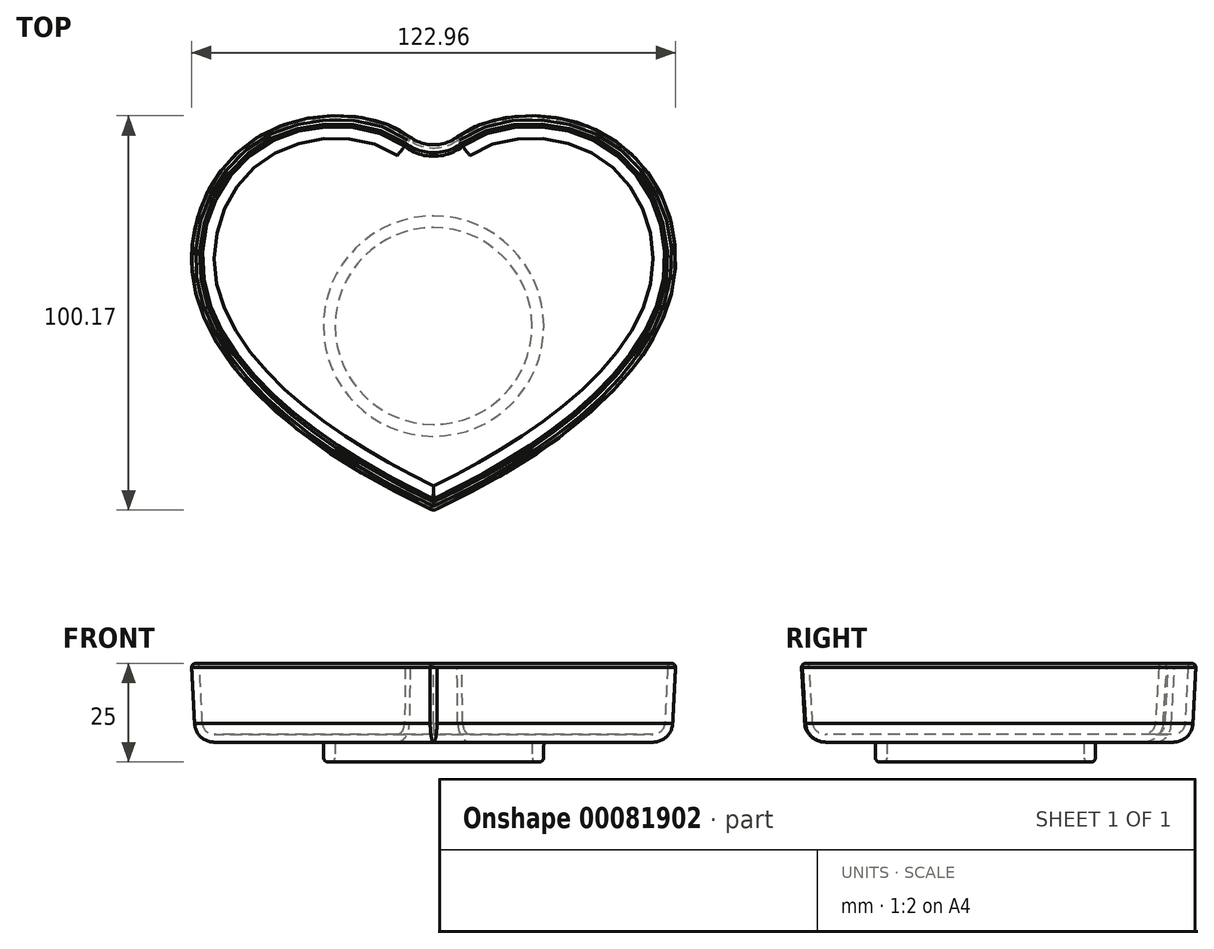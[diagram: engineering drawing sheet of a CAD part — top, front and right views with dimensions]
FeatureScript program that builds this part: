
annotation { "Feature Type Name" : "Feature", "Feature Type Description" : "" }
export const myFeature = defineFeature(function(context is Context, id is Id, definition is map)
    precondition{}
    {
        {
            var Q0;
            Q0=qCreatedBy(makeId("Top.planeOp"),FACE);
            var sketch = newSketch(context, id + "F0", { "sketchPlane" : qUnion([Q0])});
            skLineSegment(sketch, "E0", {"start": v(0, 0) * mm, "end": v(0, 80) * mm, "construction": true});
            skFitSpline(sketch, "E1", {"points": [v(0, 80) * mm, v(-38, 96) * mm, v(-60, 57) * mm, v(0, 0) * mm], "startDerivative": vector(0, 176.4) * mm, "endDerivative": vector(234.37, -109.86) * mm});
            skFitSpline(sketch, "E2.MirrorCS", {"points": [v(0, 80) * mm, v(38, 96) * mm, v(60, 57) * mm, v(0, 0) * mm], "startDerivative": vector(0, 176.4) * mm, "endDerivative": vector(-234.37, -109.86) * mm});
            skSolve(sketch);
        }
        {
            var Q0;
            Q0 = qSketchRegion(id + "F0", true);
            extrude(context, id + "F1", {"entities" : qUnion([Q0]), "depth" : 20 * mm, "hasDraft" : true, "draftAngle" : 3 * degree});
        }
        {
            var Q0;
            {var subQ0=sQuery(id+"F0.wireOp",EDGE,"E2.MirrorCS");var subQ1=sQuery(id+"F0.wireOp",EDGE,"E1");Q0=makeQuery(id+"F1.opExtrude","SWEPT_EDGE",EDGE,{"disambiguationData":[OSD([subQ1,subQ0]),TDD([makeQuery(id+"F0.imprint","INTERSECT",VERTEX,{"disambiguationData":[OD(0.0)],"derivedFrom":[subQ1,subQ0]})])]});}
            fillet(context, id + "F2", {"entities" : qUnion([Q0]), "radius" : 2 * mm, "tangentPropagation" : true, "rho" : 0.5, "crossSection" : FilletCrossSection.CONIC, "allowEdgeOverflow" : false});
        }
        {
            var Q0;
            {var subQ0=sQuery(id+"F0.wireOp",EDGE,"E2.MirrorCS");var subQ1=sQuery(id+"F0.wireOp",EDGE,"E1");Q0=makeQuery(id+"F1.opExtrude","SWEPT_EDGE",EDGE,{"disambiguationData":[OSD([subQ1,subQ0]),TDD([makeQuery(id+"F0.imprint","INTERSECT",VERTEX,{"disambiguationData":[OD(1.0)],"derivedFrom":[subQ1,subQ0]})])]});}
            fillet(context, id + "F3", {"entities" : qUnion([Q0]), "radius" : 10 * mm, "tangentPropagation" : true, "allowEdgeOverflow" : false});
        }
        {
            var Q0;
            Q0=makeQuery(id+"F1.opExtrude","CAP_FACE",FACE,{"disambiguationData":[OSD([sQuery(id+"F0.wireOp",EDGE,"E1"),sQuery(id+"F0.wireOp",EDGE,"E2.MirrorCS")])],"isStart":false});
            shell(context, id + "F4", {"entities" : qUnion([Q0]), "thickness" : 2 * mm});
        }
        {
            var Q0;
            {var subQ0=sQuery(id+"F0.wireOp",EDGE,"E1");Q0=makeQuery(id+"F4.opShell","OFFSET_EDGE",EDGE,{"disambiguationData":[OSD([subQ0]),TDD([makeQuery(id+"F1.opExtrude","CAP_EDGE",EDGE,{"disambiguationData":[OSD([subQ0])],"isStart":true})])]});}
            fillet(context, id + "F5", {"entities" : qUnion([Q0]), "radius" : 3 * mm, "tangentPropagation" : true, "allowEdgeOverflow" : false});
        }
        {
            var Q0;
            Q0=makeQuery(id+"F1.opExtrude","CAP_EDGE",EDGE,{"disambiguationData":[OSD([sQuery(id+"F0.wireOp",EDGE,"E1")])],"isStart":true});
            var Q1;
            {var subQ0=sQuery(id+"F0.wireOp",EDGE,"E2.MirrorCS");var subQ1=sQuery(id+"F0.wireOp",EDGE,"E1");Q1=makeQuery(id+"F3.opFillet","BLEND_EDGE",EDGE,{"blendedFrom":[makeQuery(id+"F1.opExtrude","SWEPT_EDGE",EDGE,{"disambiguationData":[OSD([subQ1,subQ0]),TDD([makeQuery(id+"F0.imprint","INTERSECT",VERTEX,{"disambiguationData":[OD(1.0)],"derivedFrom":[subQ1,subQ0]})])]}),makeQuery(id+"F1.opExtrude","CAP_FACE",FACE,{"disambiguationData":[OSD([subQ1,subQ0])],"isStart":true})],"blendedInto":[makeQuery(id+"F1.opExtrude","CAP_FACE",FACE,{"disambiguationData":[OSD([subQ1,subQ0])],"isStart":true})]});}
            var Q2;
            Q2=makeQuery(id+"F1.opExtrude","CAP_EDGE",EDGE,{"disambiguationData":[OSD([sQuery(id+"F0.wireOp",EDGE,"E2.MirrorCS")])],"isStart":true});
            var Q3;
            {var subQ0=sQuery(id+"F0.wireOp",EDGE,"E2.MirrorCS");var subQ1=sQuery(id+"F0.wireOp",EDGE,"E1");Q3=makeQuery(id+"F2.opFillet","BLEND_EDGE",EDGE,{"blendedFrom":[makeQuery(id+"F1.opExtrude","SWEPT_EDGE",EDGE,{"disambiguationData":[OSD([subQ1,subQ0]),TDD([makeQuery(id+"F0.imprint","INTERSECT",VERTEX,{"disambiguationData":[OD(0.0)],"derivedFrom":[subQ1,subQ0]})])]}),makeQuery(id+"F1.opExtrude","CAP_FACE",FACE,{"disambiguationData":[OSD([subQ1,subQ0])],"isStart":true})],"blendedInto":[makeQuery(id+"F1.opExtrude","CAP_FACE",FACE,{"disambiguationData":[OSD([subQ1,subQ0])],"isStart":true})]});}
            fillet(context, id + "F6", {"entities" : qUnion([Q0, Q1, Q2, Q3]), "radius" : 5 * mm, "tangentPropagation" : true, "allowEdgeOverflow" : false});
        }
        {
            var Q0;
            Q0=makeQuery(id+"F1.opExtrude","CAP_EDGE",EDGE,{"disambiguationData":[OSD([sQuery(id+"F0.wireOp",EDGE,"E1")])],"isStart":false});
            var Q1;
            {var subQ0=sQuery(id+"F0.wireOp",EDGE,"E1");Q1=makeQuery(id+"F4.opShell","OFFSET_EDGE",EDGE,{"disambiguationData":[OSD([subQ0]),TDD([makeQuery(id+"F1.opExtrude","CAP_EDGE",EDGE,{"disambiguationData":[OSD([subQ0])],"isStart":false})])]});}
            var Q2;
            {var subQ0=sQuery(id+"F0.wireOp",EDGE,"E2.MirrorCS");var subQ1=sQuery(id+"F0.wireOp",EDGE,"E1");Q2=makeQuery(id+"F4.opShell","OFFSET_EDGE",EDGE,{"disambiguationData":[OSD([subQ1,subQ0]),TDD([makeQuery(id+"F2.opFillet","BLEND_EDGE",EDGE,{"blendedFrom":[makeQuery(id+"F1.opExtrude","SWEPT_EDGE",EDGE,{"disambiguationData":[OSD([subQ1,subQ0]),TDD([makeQuery(id+"F0.imprint","INTERSECT",VERTEX,{"disambiguationData":[OD(0.0)],"derivedFrom":[subQ1,subQ0]})])]}),makeQuery(id+"F1.opExtrude","CAP_FACE",FACE,{"disambiguationData":[OSD([subQ1,subQ0])],"isStart":false})],"blendedInto":[makeQuery(id+"F1.opExtrude","CAP_FACE",FACE,{"disambiguationData":[OSD([subQ1,subQ0])],"isStart":false})]})])]});}
            var Q3;
            {var subQ0=sQuery(id+"F0.wireOp",EDGE,"E2.MirrorCS");var subQ1=sQuery(id+"F0.wireOp",EDGE,"E1");Q3=makeQuery(id+"F4.opShell","OFFSET_EDGE",EDGE,{"disambiguationData":[OSD([subQ1,subQ0]),TDD([makeQuery(id+"F3.opFillet","BLEND_EDGE",EDGE,{"blendedFrom":[makeQuery(id+"F1.opExtrude","SWEPT_EDGE",EDGE,{"disambiguationData":[OSD([subQ1,subQ0]),TDD([makeQuery(id+"F0.imprint","INTERSECT",VERTEX,{"disambiguationData":[OD(1.0)],"derivedFrom":[subQ1,subQ0]})])]}),makeQuery(id+"F1.opExtrude","CAP_FACE",FACE,{"disambiguationData":[OSD([subQ1,subQ0])],"isStart":false})],"blendedInto":[makeQuery(id+"F1.opExtrude","CAP_FACE",FACE,{"disambiguationData":[OSD([subQ1,subQ0])],"isStart":false})]})])]});}
            fillet(context, id + "F7", {"entities" : qUnion([Q0, Q1, Q2, Q3]), "radius" : 1 * mm, "tangentPropagation" : true, "allowEdgeOverflow" : false});
        }
        {
            var Q0;
            Q0=makeQuery(id+"F1.opExtrude","CAP_FACE",FACE,{"disambiguationData":[OSD([sQuery(id+"F0.wireOp",EDGE,"E1"),sQuery(id+"F0.wireOp",EDGE,"E2.MirrorCS")])],"isStart":true});
            var sketch = newSketch(context, id + "F8", { "sketchPlane" : qUnion([Q0])});
            skCircle(sketch, "E3", {"center": v(0, -45.81) * mm, "radius": 25 * mm});
            skLineSegment(sketch, "E4", {"start": v(0, -45.81) * mm, "end": v(0, -5.81) * mm, "construction": true});
            skCircle(sketch, "E5.0", {"center": v(0, -45.81) * mm, "radius": 28 * mm});
            skSolve(sketch);
        }
        {
            var Q0;
            Q0 = qSketchRegion(id + "F8", true);
            extrude(context, id + "F9", {"entities" : qUnion([Q0]), "operationType" : NewBodyOperationType.ADD, "depth" : 5 * mm, "hasDraft" : true, "draftAngle" : 1 * degree, "draftPullDirection" : true});
        }
        {
            var Q0;
            Q0=makeQuery(id+"F9.opExtrude","CAP_EDGE",EDGE,{"disambiguationData":[OSD([sQuery(id+"F8.wireOp",EDGE,"E3")])],"isStart":false});
            var Q1;
            Q1=makeQuery(id+"F9.opExtrude","CAP_EDGE",EDGE,{"disambiguationData":[OSD([sQuery(id+"F8.wireOp",EDGE,"E5.0")])],"isStart":false});
            fillet(context, id + "F10", {"entities" : qUnion([Q0, Q1]), "radius" : 1 * mm, "tangentPropagation" : true, "allowEdgeOverflow" : false});
        }
    });
